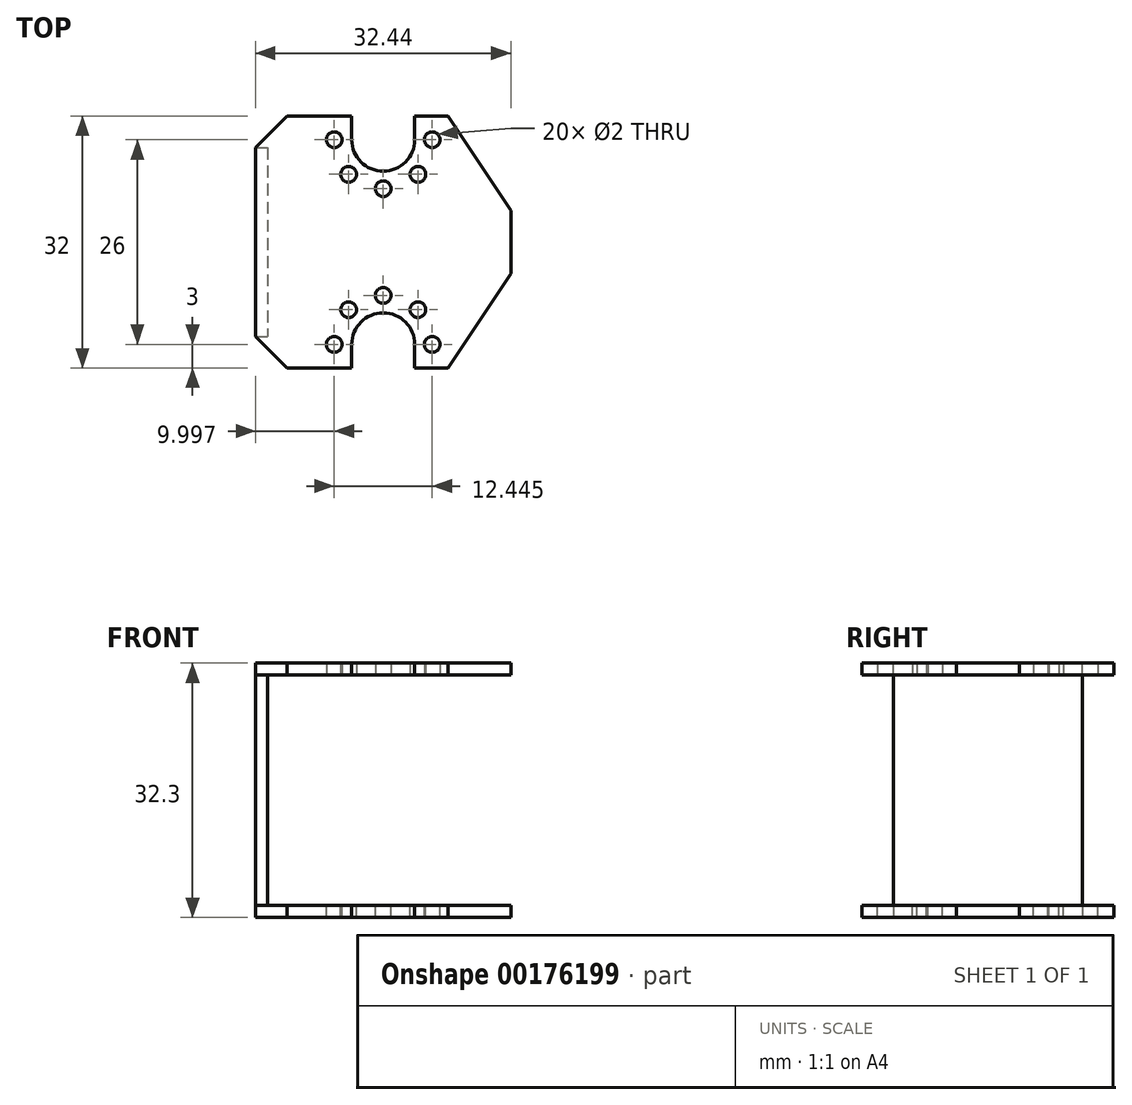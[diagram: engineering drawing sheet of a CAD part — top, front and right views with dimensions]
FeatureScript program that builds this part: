
annotation { "Feature Type Name" : "Feature", "Feature Type Description" : "" }
export const myFeature = defineFeature(function(context is Context, id is Id, definition is map)
    precondition{}
    {
        {
            var Q0;
            Q0=qCreatedBy(makeId("Top.planeOp"),FACE);
            var sketch = newSketch(context, id + "F0", { "sketchPlane" : qUnion([Q0])});
            skLineSegment(sketch, "E0.bottom", {"start": v(-16.22, 16) * mm, "end": v(-4, 16) * mm});
            skLineSegment(sketch, "E0.top", {"start": v(-16.22, -16) * mm, "end": v(-4, -16) * mm});
            skLineSegment(sketch, "E0.left", {"start": v(-16.22, 16) * mm, "end": v(-16.22, -16) * mm});
            skLineSegment(sketch, "E0.right", {"start": v(16.22, 16) * mm, "end": v(16.22, -16) * mm});
            skPoint(sketch, "E0.middle", {"position": v(0, 0) * mm});
            skArc(sketch, "E1", {"start": v(-4, 13) * mm, "mid": v(0, 9) * mm, "end": v(4, 13) * mm});
            skLineSegment(sketch, "E2.bottom", {"start": v(4.4, 8.6) * mm, "end": v(-4.4, 8.6) * mm, "construction": true});
            skLineSegment(sketch, "E2.top", {"start": v(4.4, 17.4) * mm, "end": v(-4.4, 17.4) * mm, "construction": true});
            skLineSegment(sketch, "E2.left", {"start": v(4.4, 8.6) * mm, "end": v(4.4, 17.4) * mm, "construction": true});
            skLineSegment(sketch, "E2.right", {"start": v(-4.4, 8.6) * mm, "end": v(-4.4, 17.4) * mm, "construction": true});
            skCircle(sketch, "E3", {"center": v(4.4, 8.6) * mm, "radius": 1 * mm});
            skCircle(sketch, "E4.1.0", {"center": v(6.22, 13) * mm, "radius": 1 * mm});
            skCircle(sketch, "E4.5.0", {"center": v(-6.22, 13) * mm, "radius": 1 * mm});
            skCircle(sketch, "E4.6.0", {"center": v(-4.4, 8.6) * mm, "radius": 1 * mm});
            skCircle(sketch, "E4.7.0", {"center": v(0, 6.78) * mm, "radius": 1 * mm});
            skLineSegment(sketch, "E5", {"start": v(-4, 13) * mm, "end": v(-4, 16) * mm});
            skLineSegment(sketch, "E6", {"start": v(4, 13) * mm, "end": v(4, 16) * mm});
            skLineSegment(sketch, "E7.trimOffspring", {"start": v(4, 16) * mm, "end": v(16.22, 16) * mm});
            skPoint(sketch, "E8.MirrorP", {"position": v(0, -13) * mm});
            skLineSegment(sketch, "E9.MirrorCS", {"start": v(-4, -13) * mm, "end": v(-4, -16) * mm});
            skCircle(sketch, "E10.MirrorC", {"center": v(0, -6.78) * mm, "radius": 1 * mm});
            skLineSegment(sketch, "E11.MirrorCS", {"start": v(4, -13) * mm, "end": v(4, -16) * mm});
            skCircle(sketch, "E12.MirrorC", {"center": v(-4.4, -8.6) * mm, "radius": 1 * mm});
            skCircle(sketch, "E13.MirrorC", {"center": v(6.22, -13) * mm, "radius": 1 * mm});
            skCircle(sketch, "E14.MirrorC", {"center": v(-6.22, -13) * mm, "radius": 1 * mm});
            skArc(sketch, "E15.MirrorCS", {"start": v(-4, -13) * mm, "mid": v(0, -9) * mm, "end": v(4, -13) * mm});
            skCircle(sketch, "E16.MirrorC", {"center": v(4.4, -8.6) * mm, "radius": 1 * mm});
            skLineSegment(sketch, "E17.trimOffspring", {"start": v(4, -16) * mm, "end": v(16.22, -16) * mm});
            skSolve(sketch);
        }
        {
            var Q0;
            Q0=qSketchRegion(id+"F0",true);
            extrude(context, id + "F1", {"entities" : qUnion([Q0]), "depth" : 1.5 * mm});
        }
        {
            var Q0;
            Q0=makeQuery(id+"F1.opExtrude","CAP_FACE",FACE,{"disambiguationData":[OSD([sQuery(id+"F0.wireOp",EDGE,"E0.bottom"),sQuery(id+"F0.wireOp",EDGE,"E0.top"),sQuery(id+"F0.wireOp",EDGE,"E0.left"),sQuery(id+"F0.wireOp",EDGE,"E0.right"),sQuery(id+"F0.wireOp",EDGE,"E1"),sQuery(id+"F0.wireOp",EDGE,"E3"),sQuery(id+"F0.wireOp",EDGE,"E4.1.0"),sQuery(id+"F0.wireOp",EDGE,"E4.5.0"),sQuery(id+"F0.wireOp",EDGE,"E4.6.0"),sQuery(id+"F0.wireOp",EDGE,"E4.7.0"),sQuery(id+"F0.wireOp",EDGE,"E5"),sQuery(id+"F0.wireOp",EDGE,"E6"),sQuery(id+"F0.wireOp",EDGE,"E7.trimOffspring"),sQuery(id+"F0.wireOp",EDGE,"E9.MirrorCS"),sQuery(id+"F0.wireOp",EDGE,"E10.MirrorC"),sQuery(id+"F0.wireOp",EDGE,"E11.MirrorCS"),sQuery(id+"F0.wireOp",EDGE,"E12.MirrorC"),sQuery(id+"F0.wireOp",EDGE,"E13.MirrorC"),sQuery(id+"F0.wireOp",EDGE,"E14.MirrorC"),sQuery(id+"F0.wireOp",EDGE,"E15.MirrorCS"),sQuery(id+"F0.wireOp",EDGE,"E16.MirrorC"),sQuery(id+"F0.wireOp",EDGE,"E17.trimOffspring")])],"isStart":false});
            var sketch = newSketch(context, id + "F2", { "sketchPlane" : qUnion([Q0])});
            skPoint(sketch, "E18", {"position": v(6.22, 13) * mm});
            skPoint(sketch, "E19", {"position": v(6.22, -13) * mm});
            skLineSegment(sketch, "E20", {"start": v(8.22, 16) * mm, "end": v(16.22, 4) * mm});
            skLineSegment(sketch, "E21", {"start": v(16.22, 4) * mm, "end": v(16.22, 16) * mm});
            skLineSegment(sketch, "E22", {"start": v(16.22, 16) * mm, "end": v(8.22, 16) * mm});
            skLineSegment(sketch, "E23.MirrorCS", {"start": v(16.22, -16) * mm, "end": v(8.22, -16) * mm});
            skLineSegment(sketch, "E24.MirrorCS", {"start": v(16.22, -4) * mm, "end": v(16.22, -16) * mm});
            skLineSegment(sketch, "E25.MirrorCS", {"start": v(8.22, -16) * mm, "end": v(16.22, -4) * mm});
            skLineSegment(sketch, "E26", {"start": v(-16.22, 16) * mm, "end": v(-16.22, 12) * mm});
            skLineSegment(sketch, "E27", {"start": v(-16.22, 12) * mm, "end": v(-12.22, 16) * mm});
            skLineSegment(sketch, "E28", {"start": v(-12.22, 16) * mm, "end": v(-16.22, 16) * mm});
            skLineSegment(sketch, "E29.MirrorCS", {"start": v(-12.22, -16) * mm, "end": v(-16.22, -16) * mm});
            skLineSegment(sketch, "E30.MirrorCS", {"start": v(-16.22, -12) * mm, "end": v(-12.22, -16) * mm});
            skLineSegment(sketch, "E31.MirrorCS", {"start": v(-16.22, -16) * mm, "end": v(-16.22, -12) * mm});
            skSolve(sketch);
        }
        {
            var Q0;
            Q0=qSketchRegion(id+"F2",true);
            extrude(context, id + "F3", {"entities" : qUnion([Q0]), "operationType" : NewBodyOperationType.REMOVE, "endBound" : BoundingType.UP_TO_NEXT, "oppositeDirection" : true, "depth" : 25 * mm});
        }
        {
            var Q0;
            Q0=makeQuery(id+"F1.opExtrude","CAP_FACE",FACE,{"disambiguationData":[OSD([sQuery(id+"F0.wireOp",EDGE,"E0.bottom"),sQuery(id+"F0.wireOp",EDGE,"E0.top"),sQuery(id+"F0.wireOp",EDGE,"E0.left"),sQuery(id+"F0.wireOp",EDGE,"E0.right"),sQuery(id+"F0.wireOp",EDGE,"E1"),sQuery(id+"F0.wireOp",EDGE,"E3"),sQuery(id+"F0.wireOp",EDGE,"E4.1.0"),sQuery(id+"F0.wireOp",EDGE,"E4.5.0"),sQuery(id+"F0.wireOp",EDGE,"E4.6.0"),sQuery(id+"F0.wireOp",EDGE,"E4.7.0"),sQuery(id+"F0.wireOp",EDGE,"E5"),sQuery(id+"F0.wireOp",EDGE,"E6"),sQuery(id+"F0.wireOp",EDGE,"E7.trimOffspring"),sQuery(id+"F0.wireOp",EDGE,"E9.MirrorCS"),sQuery(id+"F0.wireOp",EDGE,"E10.MirrorC"),sQuery(id+"F0.wireOp",EDGE,"E11.MirrorCS"),sQuery(id+"F0.wireOp",EDGE,"E12.MirrorC"),sQuery(id+"F0.wireOp",EDGE,"E13.MirrorC"),sQuery(id+"F0.wireOp",EDGE,"E14.MirrorC"),sQuery(id+"F0.wireOp",EDGE,"E15.MirrorCS"),sQuery(id+"F0.wireOp",EDGE,"E16.MirrorC"),sQuery(id+"F0.wireOp",EDGE,"E17.trimOffspring")])],"isStart":true});
            var sketch = newSketch(context, id + "F4", { "sketchPlane" : qUnion([Q0])});
            skLineSegment(sketch, "E32.bottom", {"start": v(-16.22, -12) * mm, "end": v(-14.72, -12) * mm});
            skLineSegment(sketch, "E32.top", {"start": v(-16.22, 12) * mm, "end": v(-14.72, 12) * mm});
            skLineSegment(sketch, "E32.left", {"start": v(-16.22, -12) * mm, "end": v(-16.22, 12) * mm});
            skLineSegment(sketch, "E32.right", {"start": v(-14.72, -12) * mm, "end": v(-14.72, 12) * mm});
            skSolve(sketch);
        }
        {
            var Q0;
            Q0=qSketchRegion(id+"F4",true);
            extrude(context, id + "F5", {"entities" : qUnion([Q0]), "operationType" : NewBodyOperationType.ADD, "depth" : (29.3 / 2) * mm});
        }
        {
            var Q0;
            Q0=qCreatedBy(makeId("Top.planeOp"),FACE);
            cPlane(context, id + "F6", {"entities" : qUnion([Q0]), "cplaneType" : CPlaneType.OFFSET, "offset" : (29.3 / 2) * mm, "oppositeDirection" : true, "width" : 150 * mm, "height" : 150 * mm});
        }
        {
            var Q0;
            Q0=makeQuery(id+"F1.opExtrude","SWEPT_BODY",BODY,{"disambiguationData":[OSD([sQuery(id+"F0.wireOp",EDGE,"E0.bottom"),sQuery(id+"F0.wireOp",EDGE,"E0.top"),sQuery(id+"F0.wireOp",EDGE,"E0.left"),sQuery(id+"F0.wireOp",EDGE,"E0.right"),sQuery(id+"F0.wireOp",EDGE,"E1"),sQuery(id+"F0.wireOp",EDGE,"E3"),sQuery(id+"F0.wireOp",EDGE,"E4.1.0"),sQuery(id+"F0.wireOp",EDGE,"E4.5.0"),sQuery(id+"F0.wireOp",EDGE,"E4.6.0"),sQuery(id+"F0.wireOp",EDGE,"E4.7.0"),sQuery(id+"F0.wireOp",EDGE,"E5"),sQuery(id+"F0.wireOp",EDGE,"E6"),sQuery(id+"F0.wireOp",EDGE,"E7.trimOffspring"),sQuery(id+"F0.wireOp",EDGE,"E9.MirrorCS"),sQuery(id+"F0.wireOp",EDGE,"E10.MirrorC"),sQuery(id+"F0.wireOp",EDGE,"E11.MirrorCS"),sQuery(id+"F0.wireOp",EDGE,"E12.MirrorC"),sQuery(id+"F0.wireOp",EDGE,"E13.MirrorC"),sQuery(id+"F0.wireOp",EDGE,"E14.MirrorC"),sQuery(id+"F0.wireOp",EDGE,"E15.MirrorCS"),sQuery(id+"F0.wireOp",EDGE,"E16.MirrorC"),sQuery(id+"F0.wireOp",EDGE,"E17.trimOffspring")])]});
            var Q1;
            Q1=qCreatedBy(id+"F6.planeOp",FACE);
            mirror(context, id + "F7", {"operationType" : NewBodyOperationType.ADD, "entities" : qUnion([Q0]), "mirrorPlane" : qUnion([Q1])});
        }
    });
